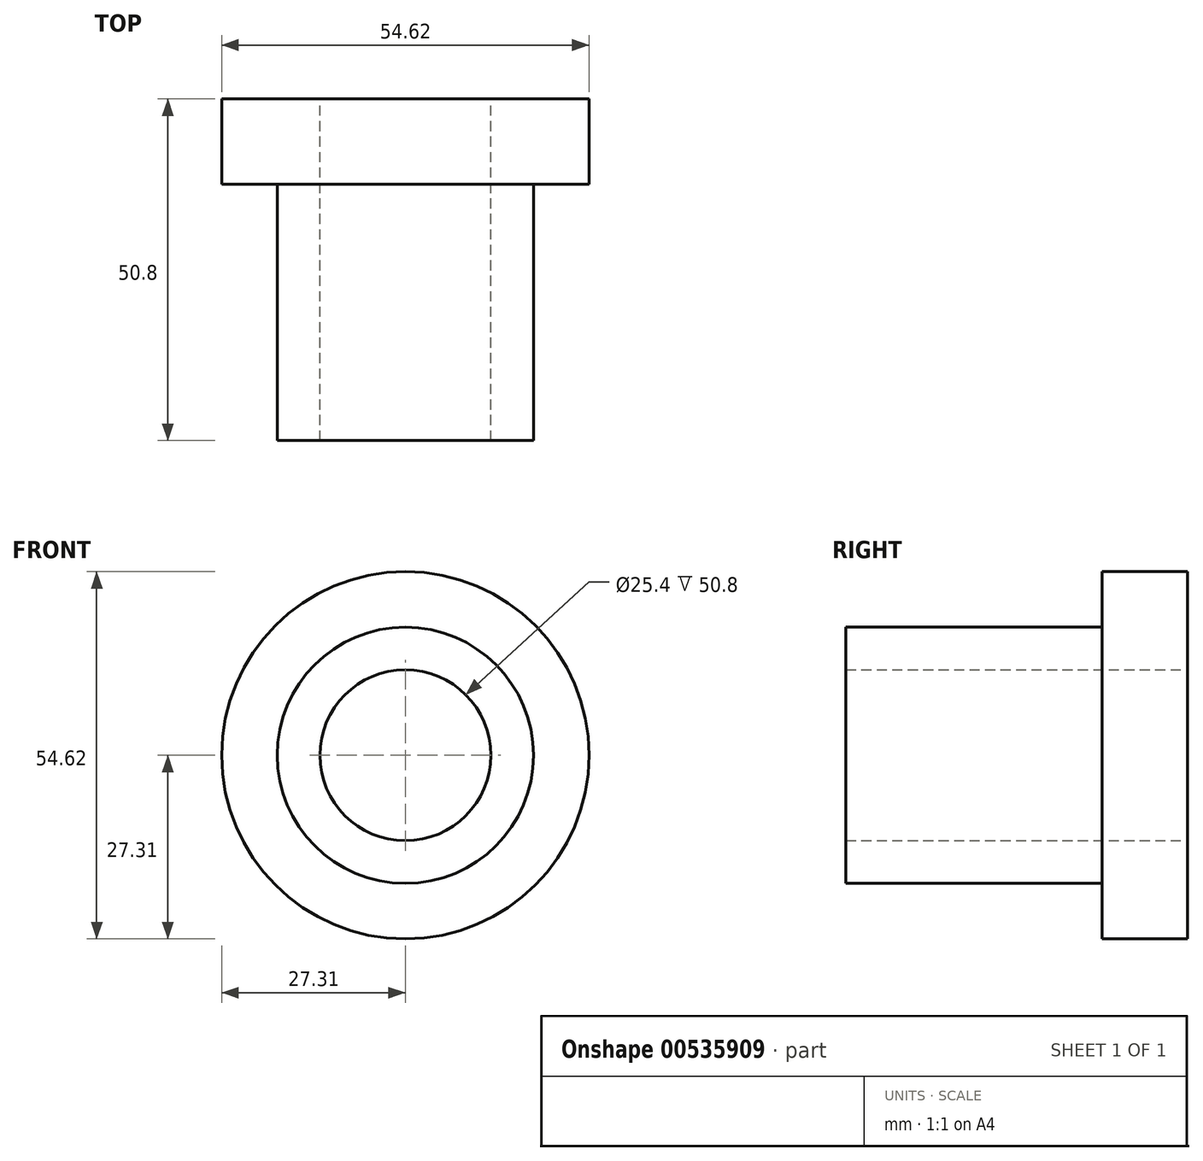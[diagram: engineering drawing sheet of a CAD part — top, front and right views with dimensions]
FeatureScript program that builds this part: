
annotation { "Feature Type Name" : "Feature", "Feature Type Description" : "" }
export const myFeature = defineFeature(function(context is Context, id is Id, definition is map)
    precondition{}
    {
        {
            var Q0;
            Q0=qCreatedBy(makeId("Front.planeOp"),FACE);
            var sketch = newSketch(context, id + "F0", { "sketchPlane" : qUnion([Q0])});
            skCircle(sketch, "E0", {"center": v(0, 0) * mm, "radius": 19.05 * mm});
            skCircle(sketch, "E1", {"center": v(0, 0) * mm, "radius": 12.7 * mm});
            skSolve(sketch);
        }
        {
            var Q0;
            Q0 = qSketchRegion(id + "F0", true);
            extrude(context, id + "F1", {"entities" : qUnion([Q0]), "depth" : 50.8 * mm, "offsetDistance" : 25.4 * mm});
        }
        {
            var Q0;
            Q0=qCreatedBy(makeId("Front.planeOp"),FACE);
            var sketch = newSketch(context, id + "F2", { "sketchPlane" : qUnion([Q0])});
            skCircle(sketch, "E2", {"center": v(0, 0) * mm, "radius": 27.3 * mm});
            skSolve(sketch);
        }
        {
            var Q0;
            Q0 = qSketchRegion(id + "F2", true);
            extrude(context, id + "F3", {"entities" : qUnion([Q0]), "operationType" : NewBodyOperationType.ADD, "depth" : 12.7 * mm, "offsetDistance" : 25.4 * mm});
        }
        {
            var Q0;
            Q0=makeQuery(id+"F0.imprint","IMPRINT",FACE,{"disambiguationData":[TD([[makeQuery(id+"F0.imprint","IMPRINT",EDGE,{"derivedFrom":sQuery(id+"F0.wireOp",EDGE,"E1")}),1.0]])]});
            extrude(context, id + "F4", {"entities" : qUnion([Q0]), "operationType" : NewBodyOperationType.REMOVE, "depth" : 42.75 * mm, "offsetDistance" : 25.4 * mm});
        }
    });
